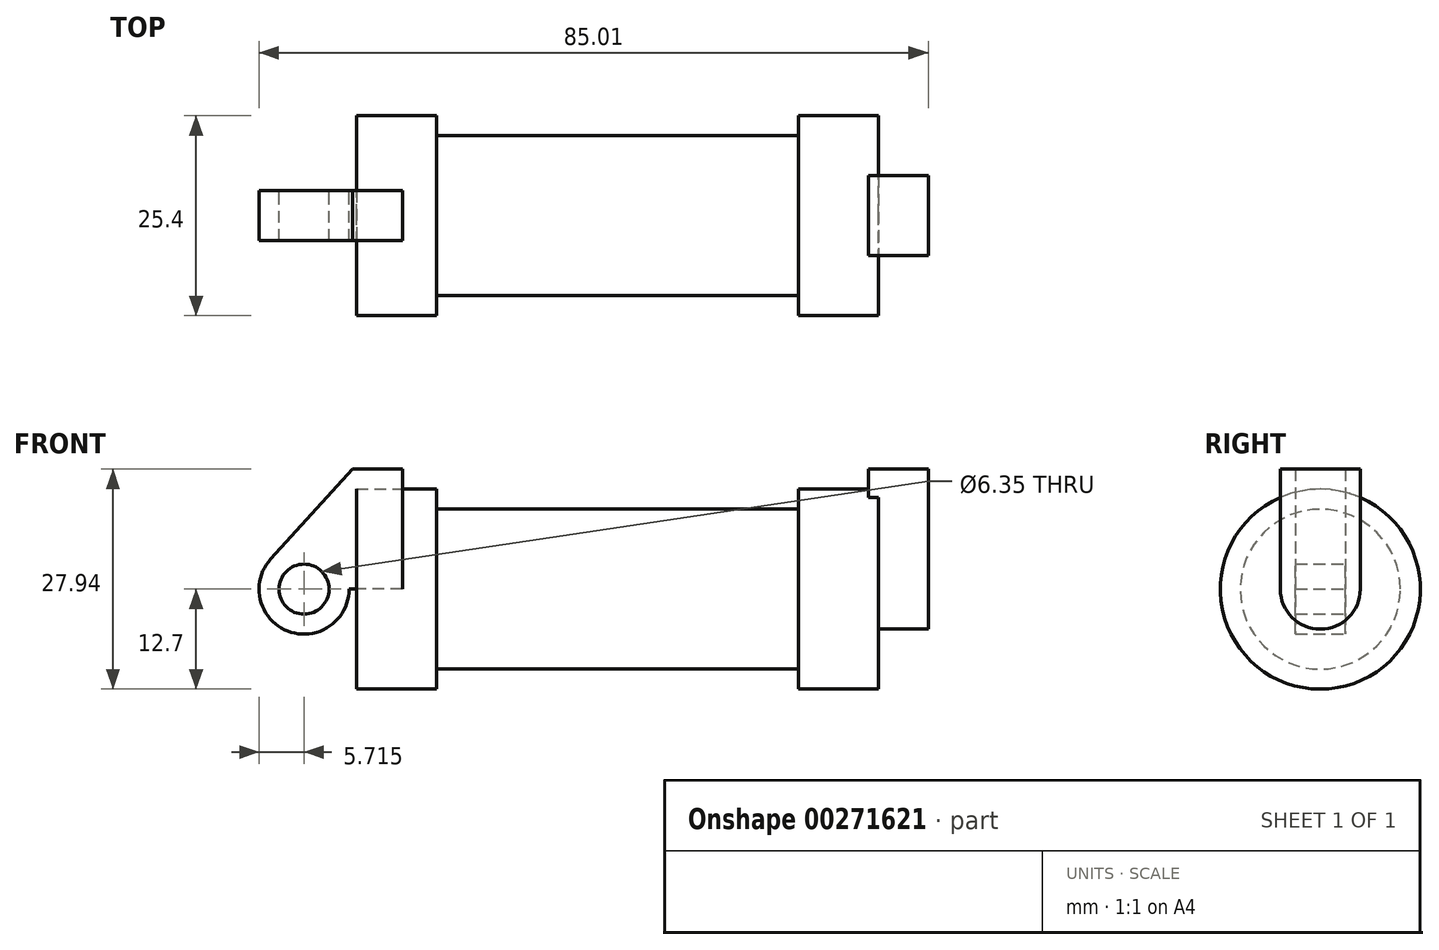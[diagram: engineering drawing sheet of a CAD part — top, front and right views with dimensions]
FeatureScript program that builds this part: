
annotation { "Feature Type Name" : "Feature", "Feature Type Description" : "" }
export const myFeature = defineFeature(function(context is Context, id is Id, definition is map)
    precondition{}
    {
        {
            var Q0;
            Q0=qCreatedBy(makeId("Front.planeOp"),FACE);
            var sketch = newSketch(context, id + "F0", { "sketchPlane" : qUnion([Q0])});
            skLineSegment(sketch, "E0", {"start": v(0, 0) * mm, "end": v(0, 12.7) * mm});
            skLineSegment(sketch, "E1", {"start": v(0, 12.7) * mm, "end": v(10.16, 12.7) * mm});
            skLineSegment(sketch, "E2", {"start": v(10.16, 12.7) * mm, "end": v(10.16, 10.16) * mm});
            skLineSegment(sketch, "E3", {"start": v(10.16, 10.16) * mm, "end": v(56.13, 10.16) * mm});
            skLineSegment(sketch, "E4", {"start": v(56.13, 10.16) * mm, "end": v(56.13, 12.7) * mm});
            skLineSegment(sketch, "E5", {"start": v(56.13, 12.7) * mm, "end": v(66.3, 12.7) * mm});
            skLineSegment(sketch, "E6", {"start": v(66.3, 12.7) * mm, "end": v(66.3, 0) * mm});
            skLineSegment(sketch, "E7", {"start": v(66.3, 0) * mm, "end": v(0, 0) * mm});
            skLineSegment(sketch, "E8", {"start": v(5.84, 15.24) * mm, "end": v(-0.5, 15.24) * mm});
            skLineSegment(sketch, "E9", {"start": v(-0.5, 15.24) * mm, "end": v(-10.88, 3.85) * mm});
            skLineSegment(sketch, "E10", {"start": v(0, 0) * mm, "end": v(-6.65, 0) * mm});
            skCircle(sketch, "E11", {"center": v(-6.65, 0) * mm, "radius": 5.72 * mm});
            skCircle(sketch, "E12", {"center": v(-6.65, 0) * mm, "radius": 3.18 * mm});
            skLineSegment(sketch, "E13", {"start": v(5.84, 15.24) * mm, "end": v(5.84, -9.4) * mm});
            skLineSegment(sketch, "E14", {"start": v(5.84, -9.4) * mm, "end": v(-8.18, -5.5) * mm});
            skSolve(sketch);
        }
        {
            var Q0;
            {var subQ0=sQuery(id+"F0.wireOp",EDGE,"E0");Q0=makeQuery(id+"F0.imprint","IMPRINT",FACE,{"disambiguationData":[TD([[makeQuery(id+"F0.imprint","IMPRINT",EDGE,{"derivedFrom":subQ0}),-1.0]])]});}
            var Q1;
            {var subQ0=sQuery(id+"F0.wireOp",EDGE,"E2");Q1=makeQuery(id+"F0.imprint","IMPRINT",FACE,{"disambiguationData":[TD([[makeQuery(id+"F0.imprint","IMPRINT",EDGE,{"derivedFrom":subQ0}),-1.0]])]});}
            var Q2;
            Q2=sQuery(id+"F0.wireOp",EDGE,"E7");
            revolve(context, id + "F1", {"entities" : qUnion([Q0, Q1]), "axis" : qUnion([Q2]), "revolveType" : RevolveType.FULL});
        }
        {
            var Q0;
            Q0=makeQuery(id+"F1.opRevolve","SWEPT_FACE",FACE,{"disambiguationData":[OSD([sQuery(id+"F0.wireOp",EDGE,"E6")])]});
            var sketch = newSketch(context, id + "F2", { "sketchPlane" : qUnion([Q0])});
            skCircle(sketch, "E15", {"center": v(0, 0) * mm, "radius": 1.52 * mm});
            skCircle(sketch, "E16", {"center": v(0, 0) * mm, "radius": 5.08 * mm});
            skLineSegment(sketch, "E17", {"start": v(-5.08, 0) * mm, "end": v(-5.08, 15.24) * mm});
            skLineSegment(sketch, "E18", {"start": v(5.08, 0) * mm, "end": v(5.08, 15.24) * mm});
            skLineSegment(sketch, "E19", {"start": v(-5.08, 15.24) * mm, "end": v(5.08, 15.24) * mm});
            skSolve(sketch);
        }
        {
            var Q0;
            {var subQ0=sQuery(id+"F2.wireOp",EDGE,"E17");var subQ1=sQuery(id+"F2.wireOp",EDGE,"E16");var subQ2=makeQuery(id+"F2.imprint","INTERSECT",VERTEX,{"derivedFrom":[subQ1,subQ0]});Q0=makeQuery(id+"F2.imprint","IMPRINT",FACE,{"disambiguationData":[TD([[makeQuery(id+"F2.imprint","IMPRINT",EDGE,{"disambiguationData":[TD([[subQ2,1.0]])],"derivedFrom":subQ1}),-1.0]])]});}
            var Q1;
            {var subQ0=sQuery(id+"F2.wireOp",EDGE,"E19");Q1=makeQuery(id+"F2.imprint","IMPRINT",FACE,{"disambiguationData":[TD([[makeQuery(id+"F2.imprint","IMPRINT",EDGE,{"derivedFrom":subQ0}),-1.0]])]});}
            var Q2;
            Q2=makeQuery(id+"F2.imprint","IMPRINT",FACE,{"disambiguationData":[TD([[makeQuery(id+"F2.imprint","IMPRINT",EDGE,{"derivedFrom":sQuery(id+"F2.wireOp",EDGE,"E15")}),-1.0]])]});
            var Q3;
            Q3=makeQuery(id+"F2.imprint","IMPRINT",FACE,{"disambiguationData":[TD([[makeQuery(id+"F2.imprint","IMPRINT",EDGE,{"derivedFrom":sQuery(id+"F2.wireOp",EDGE,"E15")}),1.0]])]});
            extrude(context, id + "F3", {"entities" : qUnion([Q0, Q1, Q2, Q3]), "operationType" : NewBodyOperationType.ADD, "depth" : 6.35 * mm, "hasSecondDirection" : true, "secondDirectionOppositeDirection" : true, "secondDirectionDepth" : 1.27 * mm});
        }
        {
            var Q0;
            Q0=sQuery(id+"F2.wireOp",EDGE,"E15");
            extrude(context, id + "F4", {"bodyType" : ToolBodyType.SURFACE, "surfaceEntities" : qUnion([Q0]), "oppositeDirection" : true, "depth" : 62.74 * mm});
        }
        {
            var Q0;
            {var subQ1=sQuery(id+"F0.wireOp",EDGE,"E0");Q0=makeQuery(id+"F0.imprint","IMPRINT",FACE,{"disambiguationData":[TD([[makeQuery(id+"F0.imprint","IMPRINT",EDGE,{"derivedFrom":subQ1}),1.0]])]});}
            var Q1;
            {var subQ5=sQuery(id+"F0.wireOp",EDGE,"E12");Q1=makeQuery(id+"F0.imprint","IMPRINT",FACE,{"disambiguationData":[TD([[makeQuery(id+"F0.imprint","IMPRINT",EDGE,{"derivedFrom":subQ5}),-1.0]])]});}
            var Q2;
            {var subQ0=sQuery(id+"F0.wireOp",EDGE,"E0");Q2=makeQuery(id+"F0.imprint","IMPRINT",FACE,{"disambiguationData":[TD([[makeQuery(id+"F0.imprint","IMPRINT",EDGE,{"derivedFrom":subQ0}),-1.0]])]});}
            extrude(context, id + "F5", {"entities" : qUnion([Q0, Q1, Q2]), "endBound" : BoundingType.SYMMETRIC, "depth" : 6.35 * mm});
        }
    });
